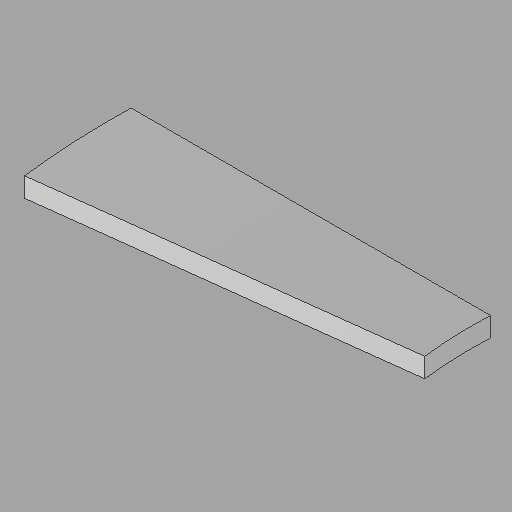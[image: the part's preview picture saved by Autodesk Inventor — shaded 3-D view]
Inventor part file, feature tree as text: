
AUTODESK INVENTOR PART (.ipt)
format: ipt  version: 2022.2 (Build 262287010, 287A)  size: 112,128 bytes
history: native  units: in
note: dims shown in document units (in); Inventor stores cm internally (conversion verified against a paired STEP export)
features: direct_edit x1, revolve x1
ambient origin geometry x8: Origin, YZ Plane, XZ Plane, XY Plane, X Axis, Y Axis, Z Axis, Center Point
bodies: Solid1 (feature_tree)
feature tree (2):
  direct_edit  "Direct Edit1"
  revolve  "Rotate1"  [1 undecoded]
note: 1 required parameter value undecoded (feature->parameter linkage not recoverable at this tier; creation-order binding heuristic only, values carry confidence <= 0.55)
